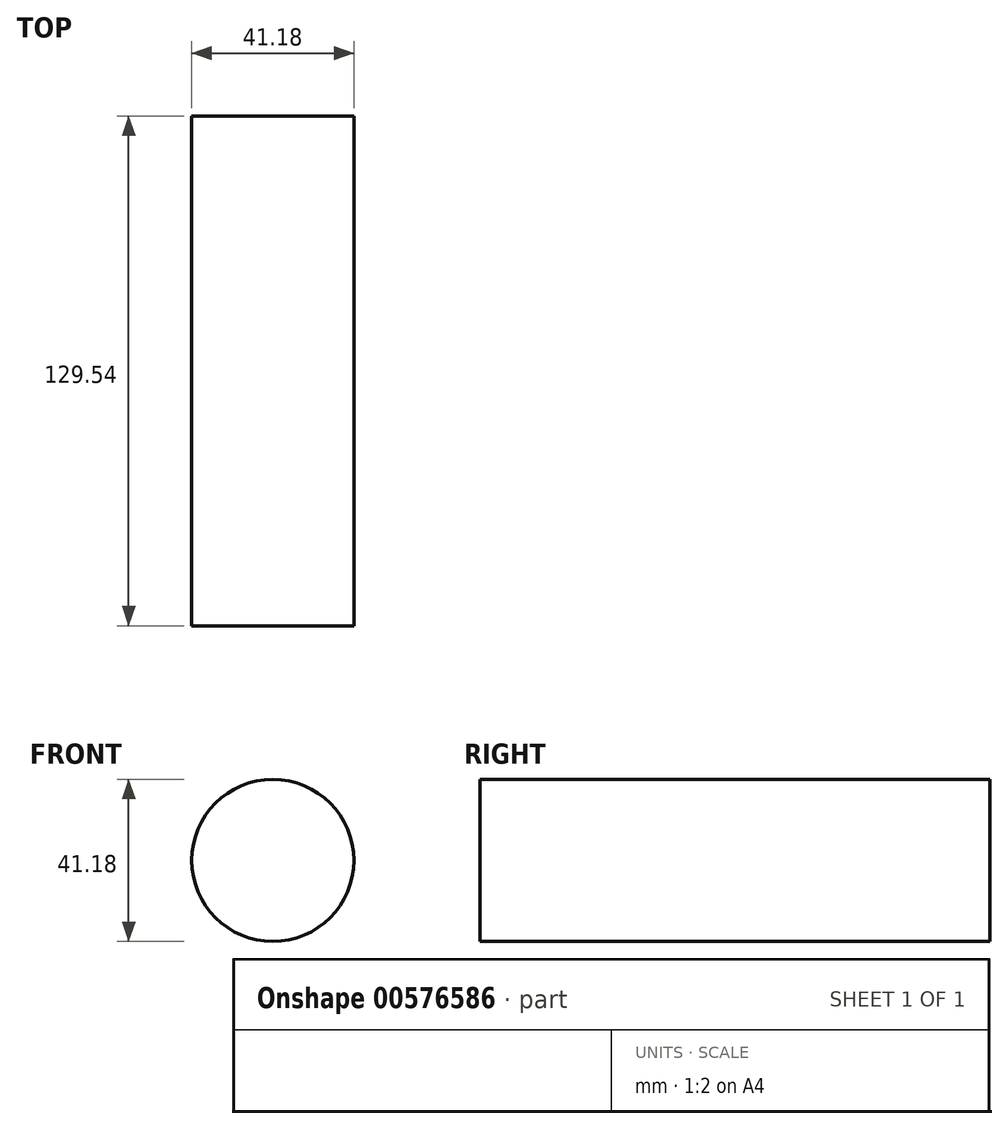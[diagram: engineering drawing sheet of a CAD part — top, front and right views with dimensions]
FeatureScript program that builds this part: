
annotation { "Feature Type Name" : "Feature", "Feature Type Description" : "" }
export const myFeature = defineFeature(function(context is Context, id is Id, definition is map)
    precondition{}
    {
        {
            var Q0;
            Q0=qCreatedBy(makeId("Front.planeOp"),FACE);
            var sketch = newSketch(context, id + "F0", { "sketchPlane" : qUnion([Q0])});
            skCircle(sketch, "E0", {"center": v(0, 0) * mm, "radius": 20.59 * mm});
            skSolve(sketch);
        }
        {
            var Q0;
            Q0=makeQuery(id+"F0.imprint","IMPRINT",FACE,{"disambiguationData":[TD([[makeQuery(id+"F0.imprint","IMPRINT",EDGE,{"derivedFrom":sQuery(id+"F0.wireOp",EDGE,"E0")}),1.0]])]});
            extrude(context, id + "F1", {"entities" : qUnion([Q0]), "depth" : 129.54 * mm, "offsetDistance" : 25.4 * mm});
        }
    });
